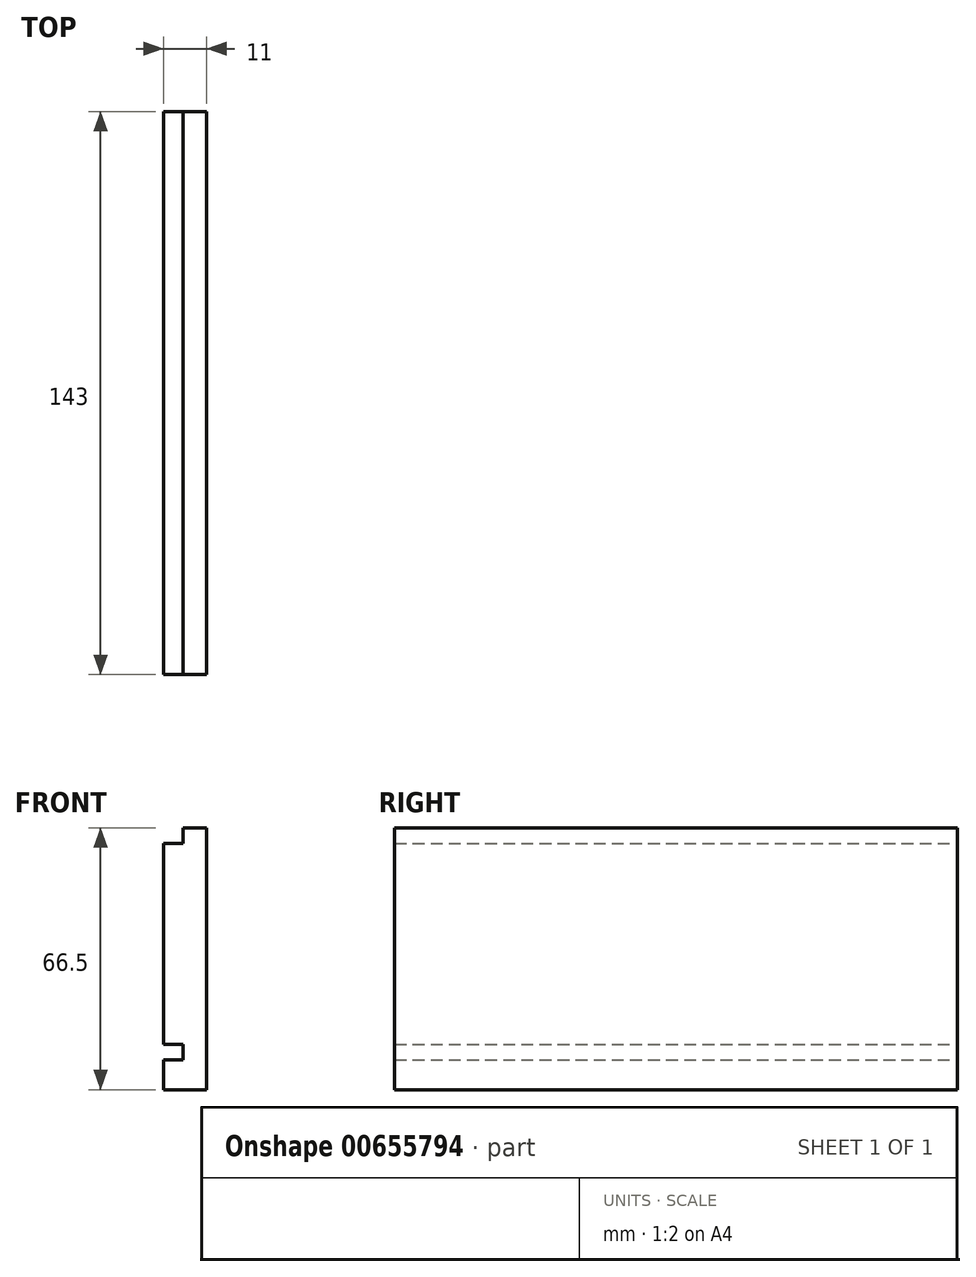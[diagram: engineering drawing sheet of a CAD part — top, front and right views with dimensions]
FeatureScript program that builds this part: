
annotation { "Feature Type Name" : "Feature", "Feature Type Description" : "" }
export const myFeature = defineFeature(function(context is Context, id is Id, definition is map)
    precondition{}
    {
        {
            var Q0;
            Q0=qCreatedBy(makeId("Front.planeOp"),FACE);
            var sketch = newSketch(context, id + "F0", { "sketchPlane" : qUnion([Q0])});
            skLineSegment(sketch, "E0", {"start": v(6.95, -35) * mm, "end": v(6.95, 34) * mm});
            skLineSegment(sketch, "E1", {"start": v(6.95, 34) * mm, "end": v(0.95, 34) * mm});
            skLineSegment(sketch, "E2", {"start": v(0.95, 30.04) * mm, "end": v(-4.05, 30.04) * mm});
            skLineSegment(sketch, "E3", {"start": v(-4.05, 30.04) * mm, "end": v(0.95, 30.04) * mm});
            skLineSegment(sketch, "E4", {"start": v(0.95, 34) * mm, "end": v(0.95, 30.04) * mm});
            skLineSegment(sketch, "E5", {"start": v(-4.05, 30.04) * mm, "end": v(-4.05, -20.96) * mm});
            skLineSegment(sketch, "E6", {"start": v(-4.05, -20.96) * mm, "end": v(0.95, -20.96) * mm});
            skLineSegment(sketch, "E7", {"start": v(0.95, -20.96) * mm, "end": v(0.95, -24.96) * mm});
            skLineSegment(sketch, "E8", {"start": v(0.95, -24.96) * mm, "end": v(-4.05, -24.96) * mm});
            skLineSegment(sketch, "E9", {"start": v(-4.05, -24.96) * mm, "end": v(-4.05, -32.5) * mm});
            skLineSegment(sketch, "E10", {"start": v(-4.05, -32.5) * mm, "end": v(6.95, -32.5) * mm});
            skSolve(sketch);
        }
        {
            var Q0;
            Q0=qSketchRegion(id+"F0",true);
            extrude(context, id + "F1", {"entities" : qUnion([Q0]), "depth" : 143 * mm, "offsetDistance" : 25 * mm});
        }
    });
